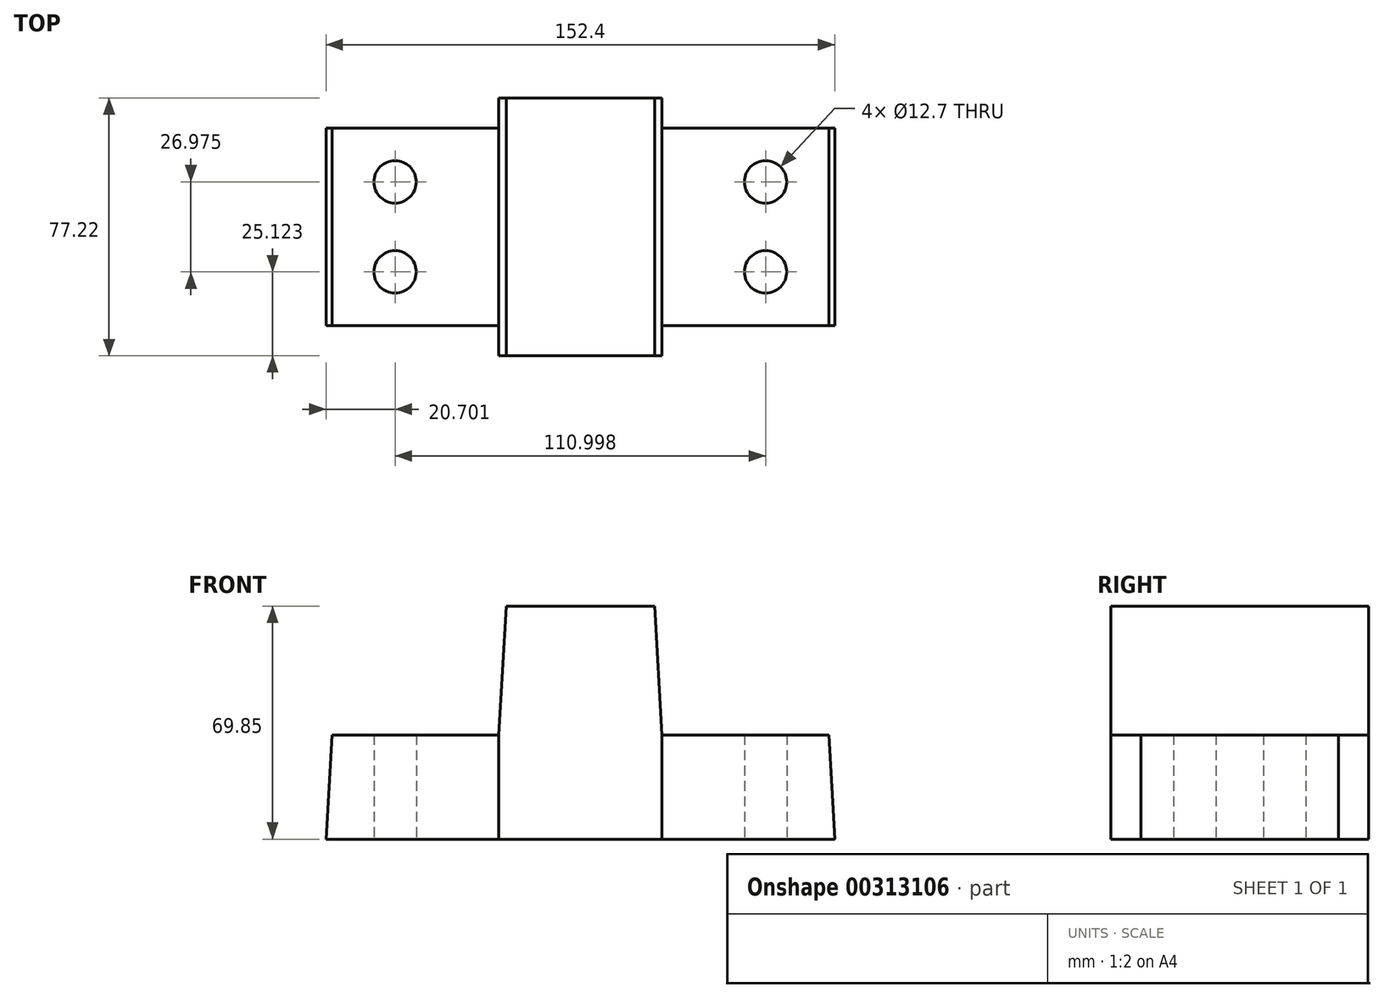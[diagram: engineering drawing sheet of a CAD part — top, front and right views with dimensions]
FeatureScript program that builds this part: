
annotation { "Feature Type Name" : "Feature", "Feature Type Description" : "" }
export const myFeature = defineFeature(function(context is Context, id is Id, definition is map)
    precondition{}
    {
        {
            var Q0;
            Q0=qCreatedBy(makeId("Front.planeOp"),FACE);
            var sketch = newSketch(context, id + "F0", { "sketchPlane" : qUnion([Q0])});
            skLineSegment(sketch, "E0", {"start": v(-76.2, 0) * mm, "end": v(76.2, 0) * mm});
            skLineSegment(sketch, "E1", {"start": v(-74.42, 31.24) * mm, "end": v(-24.42, 31.24) * mm});
            skPoint(sketch, "E2", {"position": v(0, 31.24) * mm});
            skLineSegment(sketch, "E3", {"start": v(-74.42, 31.24) * mm, "end": v(-76.2, 0) * mm});
            skLineSegment(sketch, "E4", {"start": v(74.42, 31.24) * mm, "end": v(76.2, 0) * mm});
            skLineSegment(sketch, "E5", {"start": v(-22.22, 69.85) * mm, "end": v(22.22, 69.85) * mm});
            skPoint(sketch, "E6", {"position": v(0, 69.85) * mm});
            skLineSegment(sketch, "E7", {"start": v(-22.22, 69.85) * mm, "end": v(-24.42, 31.24) * mm});
            skLineSegment(sketch, "E8", {"start": v(22.22, 69.85) * mm, "end": v(24.42, 31.24) * mm});
            skLineSegment(sketch, "E9.trimOffspring", {"start": v(24.42, 31.24) * mm, "end": v(74.42, 31.24) * mm});
            skSolve(sketch);
        }
        {
            var Q0;
            Q0 = qSketchRegion(id + "F0", true);
            extrude(context, id + "F1", {"entities" : qUnion([Q0]), "endBound" : BoundingType.SYMMETRIC, "depth" : 77.22 * mm});
        }
        {
            var Q0;
            Q0=makeQuery(id+"F1.opExtrude","SWEPT_FACE",FACE,{"disambiguationData":[OSD([sQuery(id+"F0.wireOp",EDGE,"E0")])]});
            var sketch = newSketch(context, id + "F2", { "sketchPlane" : qUnion([Q0])});
            skLineSegment(sketch, "E10.bottom", {"start": v(-76.2, 38.6) * mm, "end": v(-24.42, 38.6) * mm});
            skLineSegment(sketch, "E10.top", {"start": v(-76.2, 29.6) * mm, "end": v(-24.42, 29.6) * mm});
            skLineSegment(sketch, "E10.left", {"start": v(-76.2, 38.6) * mm, "end": v(-76.2, 29.6) * mm});
            skLineSegment(sketch, "E10.right", {"start": v(-24.42, 38.6) * mm, "end": v(-24.42, 29.6) * mm});
            skLineSegment(sketch, "E11.bottom", {"start": v(-76.2, -38.6) * mm, "end": v(-24.42, -38.6) * mm});
            skLineSegment(sketch, "E11.top", {"start": v(-76.2, -29.6) * mm, "end": v(-24.42, -29.6) * mm});
            skLineSegment(sketch, "E11.left", {"start": v(-76.2, -38.6) * mm, "end": v(-76.2, -29.6) * mm});
            skLineSegment(sketch, "E11.right", {"start": v(-24.42, -38.6) * mm, "end": v(-24.42, -29.6) * mm});
            skLineSegment(sketch, "E12.bottom", {"start": v(76.2, -38.6) * mm, "end": v(24.42, -38.6) * mm});
            skLineSegment(sketch, "E12.top", {"start": v(76.2, -29.6) * mm, "end": v(24.42, -29.6) * mm});
            skLineSegment(sketch, "E12.left", {"start": v(76.2, -38.6) * mm, "end": v(76.2, -29.6) * mm});
            skLineSegment(sketch, "E12.right", {"start": v(24.42, -38.6) * mm, "end": v(24.42, -29.6) * mm});
            skLineSegment(sketch, "E13.bottom", {"start": v(76.2, 38.6) * mm, "end": v(24.42, 38.6) * mm});
            skLineSegment(sketch, "E13.top", {"start": v(76.2, 29.6) * mm, "end": v(24.42, 29.6) * mm});
            skLineSegment(sketch, "E13.left", {"start": v(76.2, 38.6) * mm, "end": v(76.2, 29.6) * mm});
            skLineSegment(sketch, "E13.right", {"start": v(24.42, 38.6) * mm, "end": v(24.42, 29.6) * mm});
            skCircle(sketch, "E14", {"center": v(-55.5, 13.49) * mm, "radius": 6.35 * mm});
            skCircle(sketch, "E15", {"center": v(-55.5, -13.49) * mm, "radius": 6.35 * mm});
            skCircle(sketch, "E16", {"center": v(55.5, -13.49) * mm, "radius": 6.35 * mm});
            skCircle(sketch, "E17", {"center": v(55.5, 13.49) * mm, "radius": 6.35 * mm});
            skLineSegment(sketch, "E18", {"start": v(-55.5, 13.49) * mm, "end": v(-55.5, -13.49) * mm, "construction": true});
            skPoint(sketch, "E19", {"position": v(-55.5, 0) * mm});
            skLineSegment(sketch, "E20", {"start": v(-55.5, 13.49) * mm, "end": v(55.5, 13.49) * mm, "construction": true});
            skPoint(sketch, "E21", {"position": v(0, 13.49) * mm});
            skSolve(sketch);
        }
        {
            var Q0;
            Q0 = qSketchRegion(id + "F2", true);
            var Q1;
            Q1=makeQuery(id+"F1.opExtrude","SWEPT_FACE",FACE,{"disambiguationData":[OSD([sQuery(id+"F0.wireOp",EDGE,"E1")])]});
            extrude(context, id + "F3", {"entities" : qUnion([Q0]), "operationType" : NewBodyOperationType.REMOVE, "endBound" : BoundingType.UP_TO_SURFACE, "oppositeDirection" : true, "endBoundEntityFace" : qUnion([Q1]), "depth" : 25.4 * mm});
        }
    });
